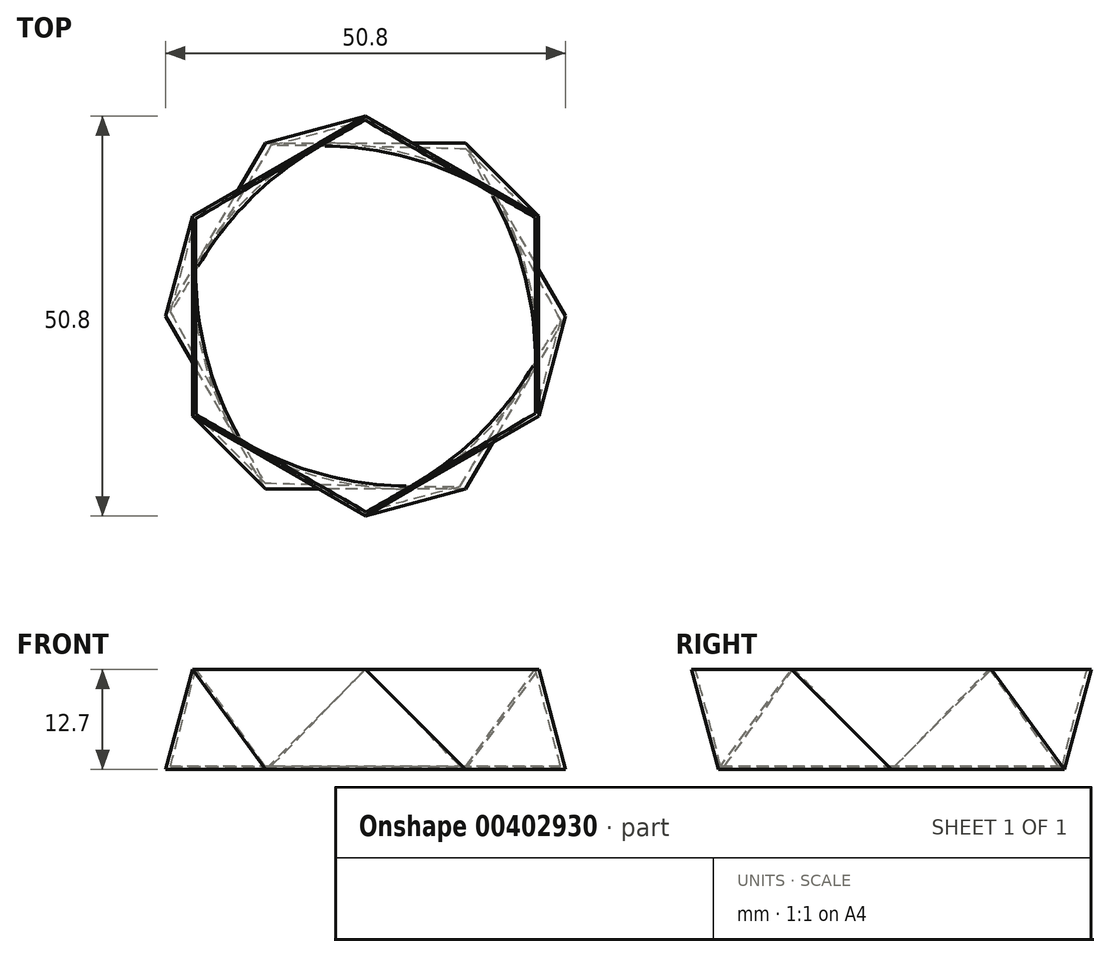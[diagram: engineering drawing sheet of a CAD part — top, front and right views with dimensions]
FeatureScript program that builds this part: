
annotation { "Feature Type Name" : "Feature", "Feature Type Description" : "" }
export const myFeature = defineFeature(function(context is Context, id is Id, definition is map)
    precondition{}
    {
        {
            var Q0;
            Q0=qCreatedBy(makeId("Top.planeOp"),FACE);
            var sketch = newSketch(context, id + "F0", { "sketchPlane" : qUnion([Q0])});
            skCircle(sketch, "E0.cCircle", {"center": v(0, 0) * mm, "radius": 22 * mm, "construction": true});
            skLineSegment(sketch, "E0.0", {"start": v(-12.7, 22) * mm, "end": v(12.7, 22) * mm});
            skLineSegment(sketch, "E0.1", {"start": v(12.7, 22) * mm, "end": v(25.4, 0) * mm});
            skLineSegment(sketch, "E0.2", {"start": v(25.4, 0) * mm, "end": v(12.7, -22) * mm});
            skLineSegment(sketch, "E0.3", {"start": v(12.7, -22) * mm, "end": v(-12.7, -22) * mm});
            skLineSegment(sketch, "E0.4", {"start": v(-12.7, -22) * mm, "end": v(-25.4, 0) * mm});
            skLineSegment(sketch, "E0.5", {"start": v(-25.4, 0) * mm, "end": v(-12.7, 22) * mm});
            skPoint(sketch, "E0.0.midPoint", {"position": v(0, 22) * mm});
            skSolve(sketch);
        }
        {
            var Q0;
            Q0=qCreatedBy(makeId("Top.planeOp"),FACE);
            cPlane(context, id + "F1", {"entities" : qUnion([Q0]), "cplaneType" : CPlaneType.OFFSET, "offset" : 12.7 * mm, "width" : 152.4 * mm, "height" : 152.4 * mm});
        }
        {
            var Q0;
            Q0=qCreatedBy(id+"F1.planeOp",FACE);
            var sketch = newSketch(context, id + "F2", { "sketchPlane" : qUnion([Q0])});
            skCircle(sketch, "E1.cCircle", {"center": v(0, 0) * mm, "radius": 22 * mm, "construction": true});
            skLineSegment(sketch, "E1.0", {"start": v(-22, 12.7) * mm, "end": v(0, 25.4) * mm});
            skLineSegment(sketch, "E1.1", {"start": v(0, 25.4) * mm, "end": v(22, 12.7) * mm});
            skLineSegment(sketch, "E1.2", {"start": v(22, 12.7) * mm, "end": v(22, -12.7) * mm});
            skLineSegment(sketch, "E1.3", {"start": v(22, -12.7) * mm, "end": v(0, -25.4) * mm});
            skLineSegment(sketch, "E1.4", {"start": v(0, -25.4) * mm, "end": v(-22, -12.7) * mm});
            skLineSegment(sketch, "E1.5", {"start": v(-22, -12.7) * mm, "end": v(-22, 12.7) * mm});
            skPoint(sketch, "E1.0.midPoint", {"position": v(-11, 19.05) * mm});
            skSolve(sketch);
        }
        {
            var Q0;
            Q0=makeQuery(id+"F0.imprint","IMPRINT",FACE,{"disambiguationData":[TD([[makeQuery(id+"F0.imprint","IMPRINT",EDGE,{"derivedFrom":sQuery(id+"F0.wireOp",EDGE,"E0.0")}),-1.0]])]});
            var Q1;
            Q1=makeQuery(id+"F2.imprint","IMPRINT",FACE,{"disambiguationData":[TD([[makeQuery(id+"F2.imprint","IMPRINT",EDGE,{"derivedFrom":sQuery(id+"F2.wireOp",EDGE,"E1.0")}),-1.0]])]});
            loft(context, id + "F3", {"sheetProfilesArray" : [{ "sheetProfileEntities" : qUnion([Q0]) }, { "sheetProfileEntities" : qUnion([Q1]) }]});
        }
        {
            var Q0;
            Q0=makeQuery(id+"F3.opLoft","CAP_FACE",FACE,{"disambiguationData":[OSD([makeQuery(id+"F2.imprint","IMPRINT",FACE,{"disambiguationData":[TD([[makeQuery(id+"F2.imprint","IMPRINT",EDGE,{"derivedFrom":sQuery(id+"F2.wireOp",EDGE,"E1.0")}),-1.0]])]})])],"isStart":true});
            shell(context, id + "F4", {"entities" : qUnion([Q0]), "thickness" : .4 * mm});
        }
    });
